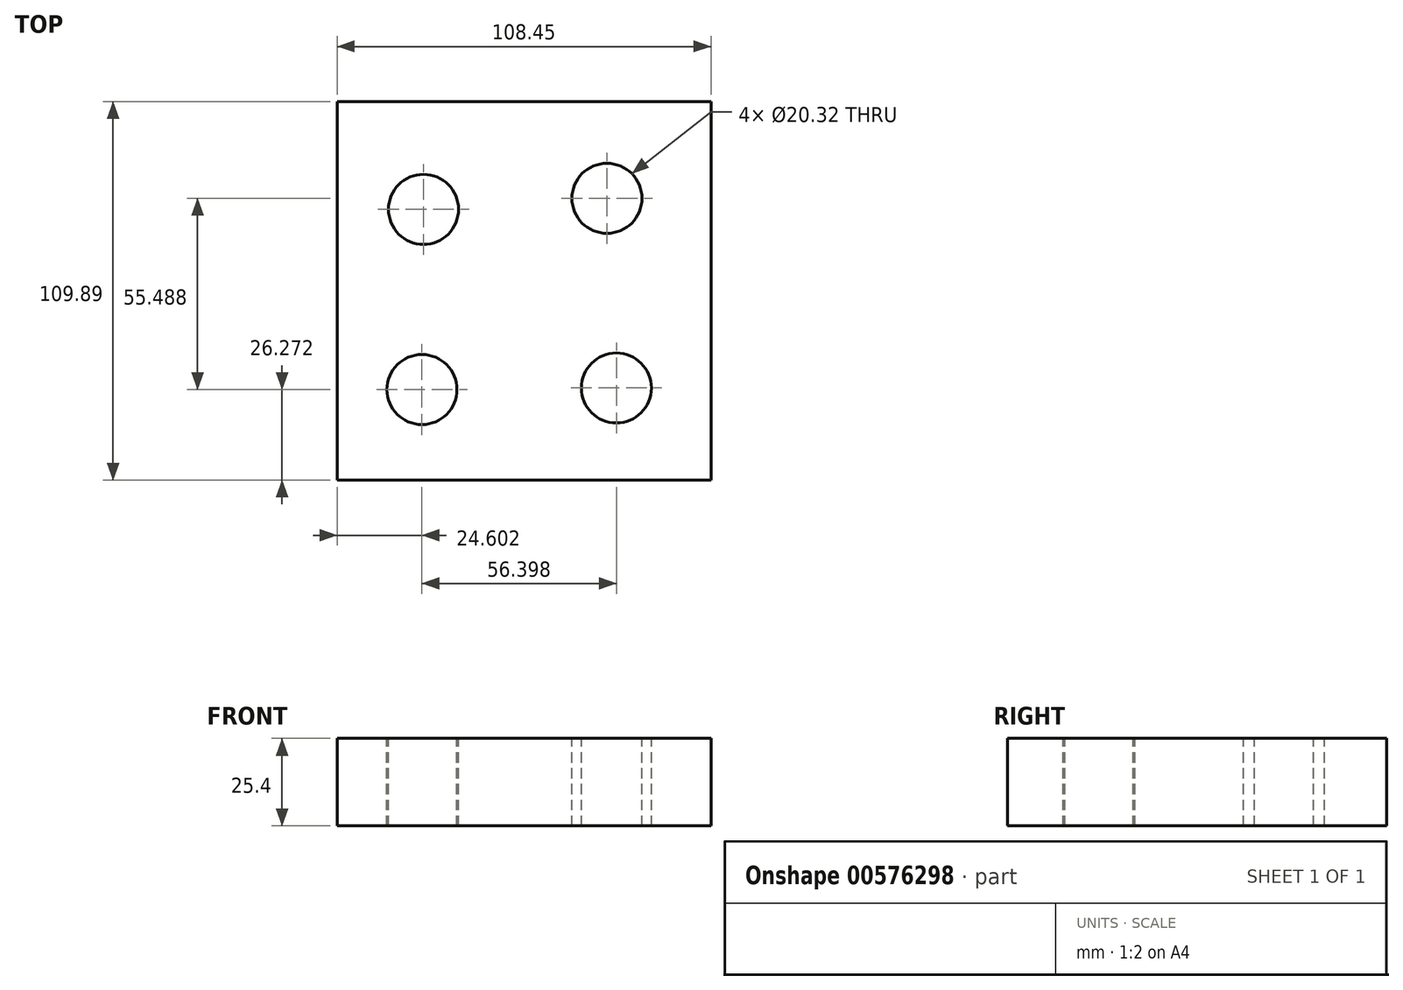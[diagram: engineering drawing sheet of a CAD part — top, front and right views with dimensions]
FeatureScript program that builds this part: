
annotation { "Feature Type Name" : "Feature", "Feature Type Description" : "" }
export const myFeature = defineFeature(function(context is Context, id is Id, definition is map)
    precondition{}
    {
        {
            var Q0;
            Q0=qCreatedBy(makeId("Top.planeOp"),FACE);
            var sketch = newSketch(context, id + "F0", { "sketchPlane" : qUnion([Q0])});
            skLineSegment(sketch, "E0.bottom", {"start": v(-53.7, -50.15) * mm, "end": v(54.74, -50.15) * mm});
            skLineSegment(sketch, "E0.top", {"start": v(-53.7, 59.74) * mm, "end": v(54.74, 59.74) * mm});
            skLineSegment(sketch, "E0.left", {"start": v(-53.7, -50.15) * mm, "end": v(-53.7, 59.74) * mm});
            skLineSegment(sketch, "E0.right", {"start": v(54.74, -50.15) * mm, "end": v(54.74, 59.74) * mm});
            skSolve(sketch);
        }
        {
            var Q0;
            Q0=makeQuery(id+"F0.imprint","IMPRINT",FACE,{"disambiguationData":[TD([[makeQuery(id+"F0.imprint","IMPRINT",EDGE,{"derivedFrom":sQuery(id+"F0.wireOp",EDGE,"E0.bottom")}),1.0]])]});
            extrude(context, id + "F1", {"entities" : qUnion([Q0]), "endBound" : BoundingType.SYMMETRIC, "depth" : 25.4 * mm, "offsetDistance" : 25.4 * mm});
        }
        {
            var Q0;
            Q0=makeQuery(id+"F1.opExtrude","CAP_FACE",FACE,{"disambiguationData":[OSD([sQuery(id+"F0.wireOp",EDGE,"E0.bottom"),sQuery(id+"F0.wireOp",EDGE,"E0.top"),sQuery(id+"F0.wireOp",EDGE,"E0.left"),sQuery(id+"F0.wireOp",EDGE,"E0.right")])],"isStart":false});
            var sketch = newSketch(context, id + "F2", { "sketchPlane" : qUnion([Q0])});
            skCircle(sketch, "E1", {"center": v(-28.65, 28.43) * mm, "radius": 14.9 * mm});
            skCircle(sketch, "E2", {"center": v(-29.1, -23.88) * mm, "radius": 14.53 * mm});
            skCircle(sketch, "E3", {"center": v(24.56, 31.61) * mm, "radius": 15.68 * mm});
            skCircle(sketch, "E4", {"center": v(27.29, -23.42) * mm, "radius": 13.86 * mm});
            skSolve(sketch);
        }
        {
            var Q0;
            Q0=sQuery(id+"F2.wireOp",VERTEX,"E1.center");
            var Q1;
            Q1=sQuery(id+"F2.wireOp",VERTEX,"E2.center");
            var Q2;
            Q2=sQuery(id+"F2.wireOp",VERTEX,"E4.center");
            var Q3;
            Q3=sQuery(id+"F2.wireOp",VERTEX,"E3.center");
            var Q4;
            Q4=makeQuery(id+"F1.opExtrude","SWEPT_BODY",BODY,{"disambiguationData":[OSD([sQuery(id+"F0.wireOp",EDGE,"E0.bottom"),sQuery(id+"F0.wireOp",EDGE,"E0.top"),sQuery(id+"F0.wireOp",EDGE,"E0.left"),sQuery(id+"F0.wireOp",EDGE,"E0.right")])]});
            hole(context, id + "F3", {"style" : HoleStyle.SIMPLE, "endStyle" : HoleEndStyle.THROUGH, "holeDiameter" : 20.32 * mm, "isTappedThrough" : true, "tappedDepth" : 12.7 * mm, "tapClearance" : 3, "locations" : qUnion([Q0, Q1, Q2, Q3]), "scope" : qUnion([Q4])});
        }
    });
